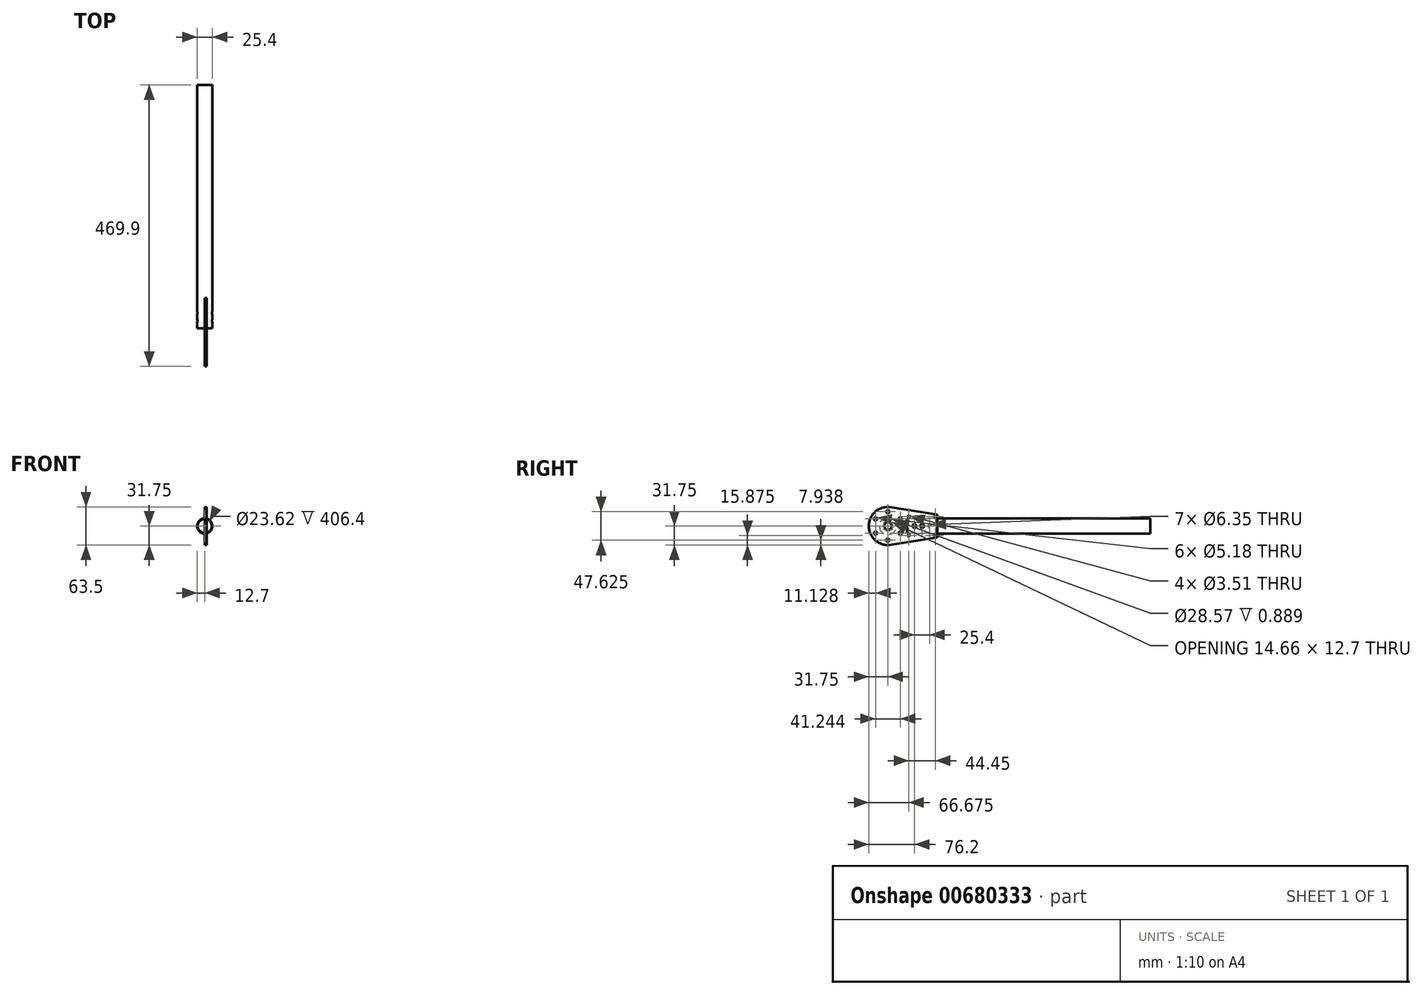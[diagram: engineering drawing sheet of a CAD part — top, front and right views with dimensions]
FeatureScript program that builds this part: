
annotation { "Feature Type Name" : "Feature", "Feature Type Description" : "" }
export const myFeature = defineFeature(function(context is Context, id is Id, definition is map)
    precondition{}
    {
        {
            var Q0;
            Q0=qCreatedBy(makeId("Front.planeOp"),FACE);
            var sketch = newSketch(context, id + "F0", { "sketchPlane" : qUnion([Q0])});
            skCircle(sketch, "E0", {"center": v(0, 0) * mm, "radius": 12.7 * mm});
            skCircle(sketch, "E1", {"center": v(0, 0) * mm, "radius": 11.81 * mm});
            skSolve(sketch);
        }
        {
            var Q0;
            Q0 = qSketchRegion(id + "F0", true);
            extrude(context, id + "F1", {"entities" : qUnion([Q0]), "oppositeDirection" : true, "depth" : 406.4 * mm, "offsetDistance" : 25.4 * mm});
        }
        {
            var Q0;
            Q0=qCreatedBy(makeId("Right.planeOp"),FACE);
            var sketch = newSketch(context, id + "F2", { "sketchPlane" : qUnion([Q0])});
            skLineSegment(sketch, "E2", {"start": v(0, 0) * mm, "end": v(91.03, 0) * mm, "construction": true});
            skCircle(sketch, "E3", {"center": v(12.7, 0) * mm, "radius": 3.18 * mm});
            skCircle(sketch, "E4", {"center": v(25.4, 0) * mm, "radius": 3.18 * mm});
            skSolve(sketch);
        }
        {
            var Q0;
            Q0 = qSketchRegion(id + "F2", true);
            extrude(context, id + "F3", {"entities" : qUnion([Q0]), "operationType" : NewBodyOperationType.REMOVE, "endBound" : BoundingType.THROUGH_ALL, "oppositeDirection" : true, "depth" : 25.4 * mm, "offsetDistance" : 25.4 * mm, "hasSecondDirection" : true, "secondDirectionOppositeDirection" : false, "secondDirectionDepth" : 25.4 * mm});
        }
        {
            var Q0;
            Q0=qCreatedBy(makeId("Right.planeOp"),FACE);
            var sketch = newSketch(context, id + "F4", { "sketchPlane" : qUnion([Q0])});
            skLineSegment(sketch, "E5.bottom", {"start": v(-31.75, 31.75) * mm, "end": v(50.8, 31.75) * mm, "construction": true});
            skLineSegment(sketch, "E5.top", {"start": v(-31.75, -31.75) * mm, "end": v(50.8, -31.75) * mm, "construction": true});
            skLineSegment(sketch, "E5.left", {"start": v(-63.5, 31.75) * mm, "end": v(-63.5, -31.75) * mm, "construction": true});
            skLineSegment(sketch, "E5.right", {"start": v(50.8, 31.75) * mm, "end": v(50.8, -31.75) * mm, "construction": true});
            skPoint(sketch, "E6", {"position": v(-63.5, 0) * mm});
            skLineSegment(sketch, "E7", {"start": v(0, 0) * mm, "end": v(-63.5, 0) * mm, "construction": true});
            skCircle(sketch, "E8.cCircle", {"center": v(-31.75, 0) * mm, "radius": 6.35 * mm, "construction": true});
            skLineSegment(sketch, "E8.0", {"start": v(-28.08, -6.35) * mm, "end": v(-35.42, -6.35) * mm});
            skLineSegment(sketch, "E8.1", {"start": v(-35.42, -6.35) * mm, "end": v(-39.08, 0) * mm});
            skLineSegment(sketch, "E8.2", {"start": v(-39.08, 0) * mm, "end": v(-35.42, 6.35) * mm});
            skLineSegment(sketch, "E8.3", {"start": v(-35.42, 6.35) * mm, "end": v(-28.08, 6.35) * mm});
            skLineSegment(sketch, "E8.4", {"start": v(-28.08, 6.35) * mm, "end": v(-24.42, 0) * mm});
            skLineSegment(sketch, "E8.5", {"start": v(-24.42, 0) * mm, "end": v(-28.08, -6.35) * mm});
            skPoint(sketch, "E8.0.midPoint", {"position": v(-31.75, -6.35) * mm});
            skCircle(sketch, "E9", {"center": v(-31.75, 0) * mm, "radius": 23.81 * mm, "construction": true});
            skLineSegment(sketch, "E10", {"start": v(-31.75, 0) * mm, "end": v(-31.75, 23.81) * mm, "construction": true});
            skPoint(sketch, "E10.endSnap0", {"position": v(-31.75, 6.35) * mm});
            skCircle(sketch, "E11", {"center": v(-31.75, 23.81) * mm, "radius": 2.6 * mm});
            skCircle(sketch, "E12.1.0", {"center": v(-52.37, 11.9) * mm, "radius": 2.6 * mm});
            skCircle(sketch, "E12.2.0", {"center": v(-52.37, -11.9) * mm, "radius": 2.6 * mm});
            skCircle(sketch, "E12.3.0", {"center": v(-31.75, -23.81) * mm, "radius": 2.6 * mm});
            skCircle(sketch, "E12.4.0", {"center": v(-11.13, -11.9) * mm, "radius": 2.6 * mm});
            skCircle(sketch, "E12.5.0", {"center": v(-11.13, 11.9) * mm, "radius": 2.6 * mm});
            skCircle(sketch, "E13", {"center": v(12.7, 0) * mm, "radius": 3.18 * mm});
            skCircle(sketch, "E14", {"center": v(25.4, 0) * mm, "radius": 3.18 * mm});
            skCircle(sketch, "E15", {"center": v(38.1, 0) * mm, "radius": 3.18 * mm});
            skLineSegment(sketch, "E16", {"start": v(47.63, 31.75) * mm, "end": v(47.63, -31.75) * mm, "construction": true});
            skLineSegment(sketch, "E17", {"start": v(50.8, 15.88) * mm, "end": v(-63.5, 15.87) * mm, "construction": true});
            skCircle(sketch, "E18", {"center": v(47.63, 15.88) * mm, "radius": 1.75 * mm});
            skCircle(sketch, "E19", {"center": v(47.63, 28.58) * mm, "radius": 1.75 * mm, "construction": true});
            skCircle(sketch, "E20.MirrorC", {"center": v(47.63, -15.88) * mm, "radius": 1.75 * mm});
            skCircle(sketch, "E21.MirrorC", {"center": v(47.63, -28.58) * mm, "radius": 1.75 * mm, "construction": true});
            skPoint(sketch, "E22", {"position": v(-6.35, 31.75) * mm});
            skLineSegment(sketch, "E23", {"start": v(-6.35, 31.75) * mm, "end": v(-6.35, -31.75) * mm, "construction": true});
            skCircle(sketch, "E24.MirrorC", {"center": v(-60.32, -28.58) * mm, "radius": 1.75 * mm, "construction": true});
            skCircle(sketch, "E25.MirrorC", {"center": v(-60.32, 28.58) * mm, "radius": 1.75 * mm, "construction": true});
            skCircle(sketch, "E26", {"center": v(-6.35, -28.57) * mm, "radius": 1.75 * mm, "construction": true});
            skCircle(sketch, "E27.MirrorC", {"center": v(-6.35, 28.57) * mm, "radius": 1.75 * mm, "construction": true});
            skArc(sketch, "E28", {"start": v(-31.75, 31.75) * mm, "mid": v(-45.95, -28.4) * mm, "end": v(-6.35, 19.05) * mm, "construction": true});
            skArc(sketch, "E29", {"start": v(-31.75, 31.75) * mm, "mid": v(-63.5, 0) * mm, "end": v(-31.75, -31.75) * mm});
            skLineSegment(sketch, "E30", {"start": v(-29.25, -31.75) * mm, "end": v(50.8, -19.05) * mm});
            skLineSegment(sketch, "E31", {"start": v(47.63, -15.88) * mm, "end": v(50.8, -15.88) * mm, "construction": true});
            skLineSegment(sketch, "E32.MirrorCS", {"start": v(-29.25, 31.75) * mm, "end": v(50.8, 19.05) * mm});
            skLineSegment(sketch, "E33", {"start": v(50.8, 19.05) * mm, "end": v(50.8, -19.05) * mm});
            skLineSegment(sketch, "E34", {"start": v(-31.75, 31.75) * mm, "end": v(-29.25, 31.75) * mm});
            skLineSegment(sketch, "E35", {"start": v(-31.75, -31.75) * mm, "end": v(-29.25, -31.75) * mm});
            skCircle(sketch, "E36", {"center": v(3.18, 15.88) * mm, "radius": 1.75 * mm});
            skCircle(sketch, "E37.MirrorC", {"center": v(3.18, -15.88) * mm, "radius": 1.75 * mm});
            skSolve(sketch);
        }
        {
            var Q0;
            Q0 = qSketchRegion(id + "F4", true);
            extrude(context, id + "F5", {"entities" : qUnion([Q0]), "depth" : 3.17 * mm, "offsetDistance" : 25.4 * mm});
        }
        {
            var Q0;
            Q0=makeQuery(id+"F5.opExtrude","CAP_FACE",FACE,{"disambiguationData":[OSD([sQuery(id+"F4.wireOp",EDGE,"E5.bottom"),sQuery(id+"F4.wireOp",EDGE,"E5.top"),sQuery(id+"F4.wireOp",EDGE,"E5.left"),sQuery(id+"F4.wireOp",EDGE,"E5.right"),sQuery(id+"F4.wireOp",EDGE,"E8.0"),sQuery(id+"F4.wireOp",EDGE,"E8.1"),sQuery(id+"F4.wireOp",EDGE,"E8.2"),sQuery(id+"F4.wireOp",EDGE,"E8.3"),sQuery(id+"F4.wireOp",EDGE,"E8.4"),sQuery(id+"F4.wireOp",EDGE,"E8.5"),sQuery(id+"F4.wireOp",EDGE,"E11"),sQuery(id+"F4.wireOp",EDGE,"E12.1.0"),sQuery(id+"F4.wireOp",EDGE,"E12.2.0"),sQuery(id+"F4.wireOp",EDGE,"E12.3.0"),sQuery(id+"F4.wireOp",EDGE,"E12.4.0"),sQuery(id+"F4.wireOp",EDGE,"E12.5.0"),sQuery(id+"F4.wireOp",EDGE,"E13"),sQuery(id+"F4.wireOp",EDGE,"E14"),sQuery(id+"F4.wireOp",EDGE,"E15"),sQuery(id+"F4.wireOp",EDGE,"E18"),sQuery(id+"F4.wireOp",EDGE,"E19"),sQuery(id+"F4.wireOp",EDGE,"SXmX5qNj-NGBv-P4yf-tPgC-NAErbAux3Ky4"),sQuery(id+"F4.wireOp",EDGE,"E20.MirrorC"),sQuery(id+"F4.wireOp",EDGE,"E21.MirrorC"),sQuery(id+"F4.wireOp",EDGE,"E24.MirrorC"),sQuery(id+"F4.wireOp",EDGE,"E25.MirrorC"),sQuery(id+"F4.wireOp",EDGE,"E26"),sQuery(id+"F4.wireOp",EDGE,"E27.MirrorC")])],"isStart":true});
            var sketch = newSketch(context, id + "F6", { "sketchPlane" : qUnion([Q0])});
            skCircle(sketch, "E38", {"center": v(31.75, 0) * mm, "radius": 14.29 * mm});
            skLineSegment(sketch, "E39", {"start": v(31.75, 6.35) * mm, "end": v(31.75, -6.35) * mm, "construction": true});
            skSolve(sketch);
        }
        {
            var Q0;
            Q0 = qSketchRegion(id + "F6", true);
            extrude(context, id + "F7", {"entities" : qUnion([Q0]), "operationType" : NewBodyOperationType.REMOVE, "oppositeDirection" : true, "depth" : 0.89 * mm, "offsetDistance" : 25.4 * mm});
        }
    });
